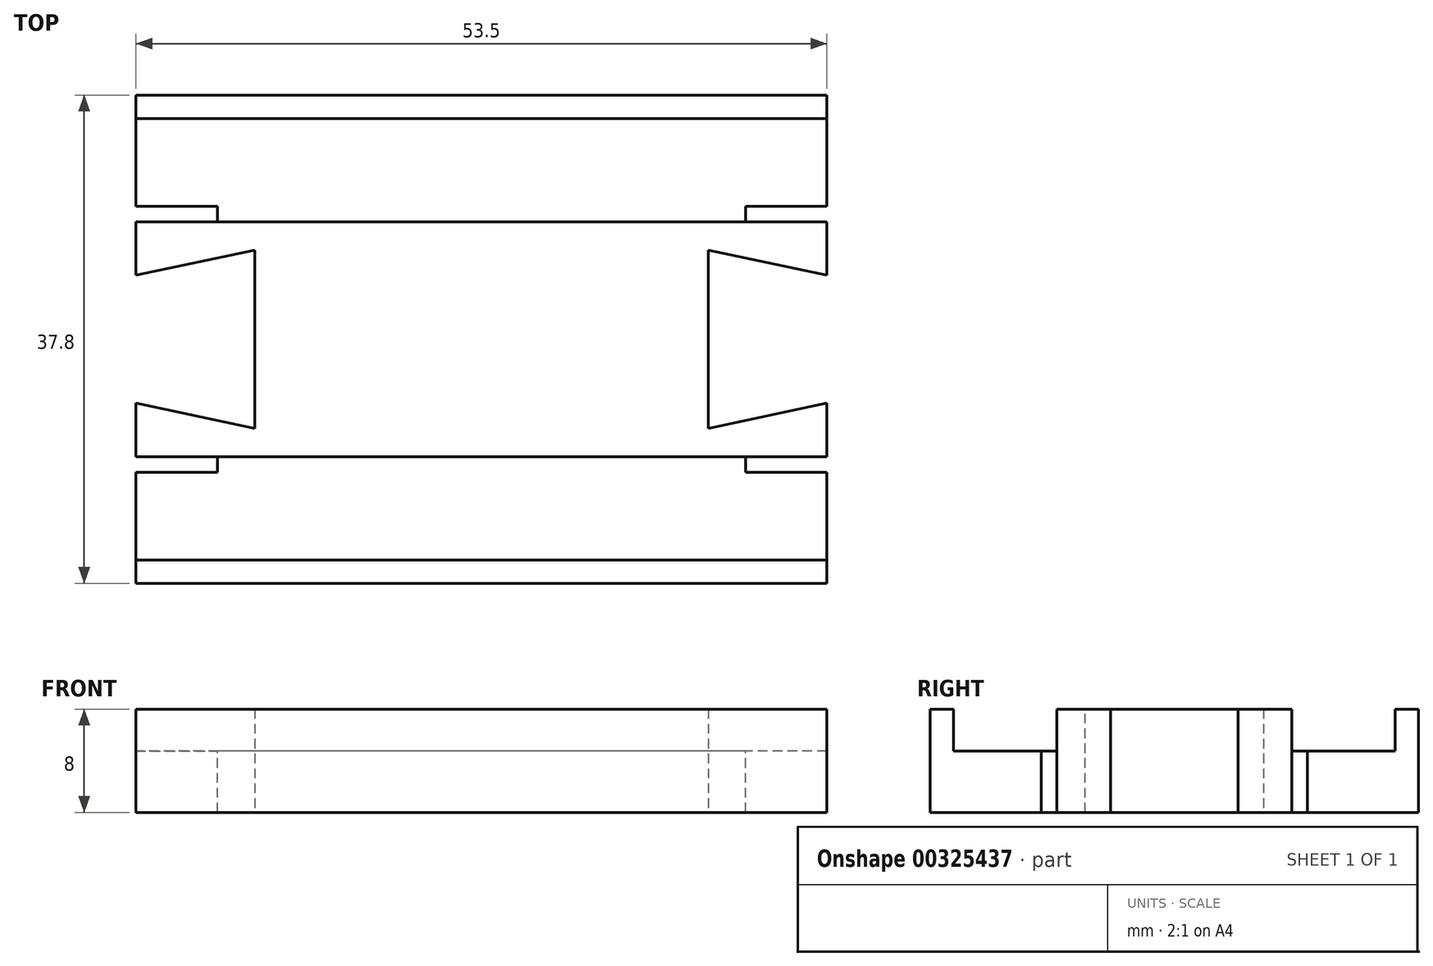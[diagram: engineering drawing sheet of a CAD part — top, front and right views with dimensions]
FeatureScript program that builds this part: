
annotation { "Feature Type Name" : "Feature", "Feature Type Description" : "" }
export const myFeature = defineFeature(function(context is Context, id is Id, definition is map)
    precondition{}
    {
        {
            var Q0;
            Q0=qCreatedBy(makeId("Top.planeOp"),FACE);
            var sketch = newSketch(context, id + "F0", { "sketchPlane" : qUnion([Q0])});
            skLineSegment(sketch, "E0.bottom", {"start": v(26.75, -18.9) * mm, "end": v(-26.75, -18.9) * mm});
            skLineSegment(sketch, "E0.top", {"start": v(26.75, 18.9) * mm, "end": v(-26.75, 18.9) * mm});
            skLineSegment(sketch, "E0.left", {"start": v(26.75, -18.9) * mm, "end": v(26.75, 18.9) * mm});
            skLineSegment(sketch, "E0.right", {"start": v(-26.75, -18.9) * mm, "end": v(-26.75, 18.9) * mm});
            skPoint(sketch, "E0.middle", {"position": v(0, 0) * mm});
            skSolve(sketch);
        }
        {
            var Q0;
            Q0=makeQuery(id+"F0.imprint","IMPRINT",FACE,{"disambiguationData":[TD([[makeQuery(id+"F0.imprint","IMPRINT",EDGE,{"derivedFrom":sQuery(id+"F0.wireOp",EDGE,"E0.bottom")}),-1.0]])]});
            extrude(context, id + "F1", {"entities" : qUnion([Q0]), "depth" : 8 * mm});
        }
        {
            var Q0;
            Q0=makeQuery(id+"F1.opExtrude","CAP_FACE",FACE,{"disambiguationData":[OSD([sQuery(id+"F0.wireOp",EDGE,"E0.bottom"),sQuery(id+"F0.wireOp",EDGE,"E0.top"),sQuery(id+"F0.wireOp",EDGE,"E0.left"),sQuery(id+"F0.wireOp",EDGE,"E0.right")])],"isStart":false});
            var sketch = newSketch(context, id + "F2", { "sketchPlane" : qUnion([Q0])});
            skLineSegment(sketch, "E1.bottom", {"start": v(26.75, 17.1) * mm, "end": v(-26.75, 17.1) * mm});
            skLineSegment(sketch, "E1.top", {"start": v(26.75, -17.1) * mm, "end": v(-26.75, -17.1) * mm});
            skLineSegment(sketch, "E1.left", {"start": v(26.75, 17.1) * mm, "end": v(26.75, -17.1) * mm});
            skLineSegment(sketch, "E1.right", {"start": v(-26.75, 17.1) * mm, "end": v(-26.75, -17.1) * mm});
            skPoint(sketch, "E1.middle", {"position": v(0, 0) * mm});
            skLineSegment(sketch, "E2.bottom", {"start": v(26.75, 9.1) * mm, "end": v(-26.75, 9.1) * mm});
            skLineSegment(sketch, "E2.top", {"start": v(26.75, -9.1) * mm, "end": v(-26.75, -9.1) * mm});
            skLineSegment(sketch, "E2.left", {"start": v(26.75, 9.1) * mm, "end": v(26.75, -9.1) * mm});
            skLineSegment(sketch, "E2.right", {"start": v(-26.75, 9.1) * mm, "end": v(-26.75, -9.1) * mm});
            skLineSegment(sketch, "E3.bottom", {"start": v(26.75, 7.7) * mm, "end": v(-26.75, 7.7) * mm});
            skLineSegment(sketch, "E3.top", {"start": v(26.75, -7.7) * mm, "end": v(-26.75, -7.7) * mm});
            skLineSegment(sketch, "E3.left", {"start": v(26.75, 7.7) * mm, "end": v(26.75, -7.7) * mm});
            skLineSegment(sketch, "E3.right", {"start": v(-26.75, 7.7) * mm, "end": v(-26.75, -7.7) * mm});
            skSolve(sketch);
        }
        {
            var Q0;
            {var subQ0=sQuery(id+"F2.wireOp",EDGE,"E1.top");Q0=makeQuery(id+"F2.imprint","IMPRINT",FACE,{"disambiguationData":[TD([[makeQuery(id+"F2.imprint","IMPRINT",EDGE,{"derivedFrom":subQ0}),-1.0]])]});}
            var Q1;
            {var subQ0=sQuery(id+"F2.wireOp",EDGE,"E1.bottom");Q1=makeQuery(id+"F2.imprint","IMPRINT",FACE,{"disambiguationData":[TD([[makeQuery(id+"F2.imprint","IMPRINT",EDGE,{"derivedFrom":subQ0}),1.0]])]});}
            extrude(context, id + "F3", {"entities" : qUnion([Q0, Q1]), "operationType" : NewBodyOperationType.REMOVE, "oppositeDirection" : true, "depth" : ((8 - 1.5) / 2) * mm});
        }
        {
            var Q0;
            Q0=makeQuery(id+"F1.opExtrude","SWEPT_FACE",FACE,{"disambiguationData":[OSD([sQuery(id+"F0.wireOp",EDGE,"E0.right")])]});
            var sketch = newSketch(context, id + "F4", { "sketchPlane" : qUnion([Q0])});
            skLineSegment(sketch, "E4.bottom", {"start": v(-4.95, 0) * mm, "end": v(4.95, 0) * mm});
            skLineSegment(sketch, "E4.top", {"start": v(-4.95, 8) * mm, "end": v(4.95, 8) * mm});
            skLineSegment(sketch, "E4.left", {"start": v(-4.95, 0) * mm, "end": v(-4.95, 8) * mm});
            skLineSegment(sketch, "E4.right", {"start": v(4.95, 0) * mm, "end": v(4.95, 8) * mm});
            skPoint(sketch, "E4.middle", {"position": v(0, 0) * mm});
            skSolve(sketch);
        }
        {
            var Q0;
            Q0=makeQuery(id+"F4.imprint","IMPRINT",FACE,{"disambiguationData":[TD([[makeQuery(id+"F4.imprint","IMPRINT",EDGE,{"derivedFrom":sQuery(id+"F4.wireOp",EDGE,"E4.bottom")}),-1.0]])]});
            extrude(context, id + "F5", {"entities" : qUnion([Q0]), "operationType" : NewBodyOperationType.REMOVE, "oppositeDirection" : true, "depth" : 9.2 * mm, "hasDraft" : true, "draftAngle" : 12 * degree});
        }
        {
            var Q0;
            Q0=makeQuery(id+"F1.opExtrude","SWEPT_FACE",FACE,{"disambiguationData":[OSD([sQuery(id+"F0.wireOp",EDGE,"E0.left")])]});
            var sketch = newSketch(context, id + "F6", { "sketchPlane" : qUnion([Q0])});
            skLineSegment(sketch, "E5.bottom", {"start": v(-4.95, 0) * mm, "end": v(4.95, 0) * mm});
            skLineSegment(sketch, "E5.top", {"start": v(-4.95, 8) * mm, "end": v(4.95, 8) * mm});
            skLineSegment(sketch, "E5.left", {"start": v(-4.95, 0) * mm, "end": v(-4.95, 8) * mm});
            skLineSegment(sketch, "E5.right", {"start": v(4.95, 0) * mm, "end": v(4.95, 8) * mm});
            skPoint(sketch, "E5.middle", {"position": v(0, 8.08) * mm});
            skSolve(sketch);
        }
        {
            var Q0;
            Q0=makeQuery(id+"F6.imprint","IMPRINT",FACE,{"disambiguationData":[TD([[makeQuery(id+"F6.imprint","IMPRINT",EDGE,{"derivedFrom":sQuery(id+"F6.wireOp",EDGE,"E5.bottom")}),1.0]])]});
            extrude(context, id + "F7", {"entities" : qUnion([Q0]), "operationType" : NewBodyOperationType.REMOVE, "oppositeDirection" : true, "depth" : 9.2 * mm, "hasDraft" : true, "draftAngle" : 12 * degree});
        }
        {
            var Q0;
            Q0=makeQuery(id+"F3.boolean.opBoolean","COPY",FACE,{"derivedFrom":makeQuery(id+"F3.opExtrude","CAP_FACE",FACE,{"disambiguationData":[OSD([sQuery(id+"F2.wireOp",EDGE,"E1.top"),sQuery(id+"F2.wireOp",EDGE,"E1.left"),sQuery(id+"F2.wireOp",EDGE,"E1.right"),sQuery(id+"F2.wireOp",EDGE,"E2.top")])],"isStart":false})});
            var sketch = newSketch(context, id + "F8", { "sketchPlane" : qUnion([Q0])});
            skLineSegment(sketch, "E6.bottom", {"start": v(26.75, -9.1) * mm, "end": v(20.45, -9.1) * mm});
            skLineSegment(sketch, "E6.top", {"start": v(26.75, -10.3) * mm, "end": v(20.45, -10.3) * mm});
            skLineSegment(sketch, "E6.left", {"start": v(26.75, -9.1) * mm, "end": v(26.75, -10.3) * mm});
            skLineSegment(sketch, "E6.right", {"start": v(20.45, -9.1) * mm, "end": v(20.45, -10.3) * mm});
            skLineSegment(sketch, "E7.bottom", {"start": v(-26.75, -9.1) * mm, "end": v(-20.45, -9.1) * mm});
            skLineSegment(sketch, "E7.top", {"start": v(-26.75, -10.3) * mm, "end": v(-20.45, -10.3) * mm});
            skLineSegment(sketch, "E7.left", {"start": v(-26.75, -9.1) * mm, "end": v(-26.75, -10.3) * mm});
            skLineSegment(sketch, "E7.right", {"start": v(-20.45, -9.1) * mm, "end": v(-20.45, -10.3) * mm});
            skSolve(sketch);
        }
        {
            var Q0;
            Q0=makeQuery(id+"F3.boolean.opBoolean","COPY",FACE,{"derivedFrom":makeQuery(id+"F3.opExtrude","CAP_FACE",FACE,{"disambiguationData":[OSD([sQuery(id+"F2.wireOp",EDGE,"E1.bottom"),sQuery(id+"F2.wireOp",EDGE,"E1.left"),sQuery(id+"F2.wireOp",EDGE,"E1.right"),sQuery(id+"F2.wireOp",EDGE,"E2.bottom")])],"isStart":false})});
            var sketch = newSketch(context, id + "F9", { "sketchPlane" : qUnion([Q0])});
            skLineSegment(sketch, "E8.bottom", {"start": v(26.75, 9.1) * mm, "end": v(20.45, 9.1) * mm});
            skLineSegment(sketch, "E8.top", {"start": v(26.75, 10.3) * mm, "end": v(20.45, 10.3) * mm});
            skLineSegment(sketch, "E8.left", {"start": v(26.75, 9.1) * mm, "end": v(26.75, 10.3) * mm});
            skLineSegment(sketch, "E8.right", {"start": v(20.45, 9.1) * mm, "end": v(20.45, 10.3) * mm});
            skLineSegment(sketch, "E9.bottom", {"start": v(-26.75, 9.1) * mm, "end": v(-20.45, 9.1) * mm});
            skLineSegment(sketch, "E9.top", {"start": v(-26.75, 10.3) * mm, "end": v(-20.45, 10.3) * mm});
            skLineSegment(sketch, "E9.left", {"start": v(-26.75, 9.1) * mm, "end": v(-26.75, 10.3) * mm});
            skLineSegment(sketch, "E9.right", {"start": v(-20.45, 9.1) * mm, "end": v(-20.45, 10.3) * mm});
            skSolve(sketch);
        }
        {
            var Q0;
            Q0=makeQuery(id+"F9.imprint","IMPRINT",FACE,{"disambiguationData":[TD([[makeQuery(id+"F9.imprint","IMPRINT",EDGE,{"derivedFrom":sQuery(id+"F9.wireOp",EDGE,"E8.bottom")}),-1.0]])]});
            var Q1;
            Q1=makeQuery(id+"F9.imprint","IMPRINT",FACE,{"disambiguationData":[TD([[makeQuery(id+"F9.imprint","IMPRINT",EDGE,{"derivedFrom":sQuery(id+"F9.wireOp",EDGE,"E9.bottom")}),-1.0]])]});
            var Q2;
            Q2=makeQuery(id+"F8.imprint","IMPRINT",FACE,{"disambiguationData":[TD([[makeQuery(id+"F8.imprint","IMPRINT",EDGE,{"derivedFrom":sQuery(id+"F8.wireOp",EDGE,"E7.bottom")}),1.0]])]});
            var Q3;
            Q3=makeQuery(id+"F8.imprint","IMPRINT",FACE,{"disambiguationData":[TD([[makeQuery(id+"F8.imprint","IMPRINT",EDGE,{"derivedFrom":sQuery(id+"F8.wireOp",EDGE,"E6.bottom")}),1.0]])]});
            extrude(context, id + "F10", {"entities" : qUnion([Q0, Q1, Q2, Q3]), "operationType" : NewBodyOperationType.REMOVE, "oppositeDirection" : true, "depth" : (8 - 3.25) * mm});
        }
    });
